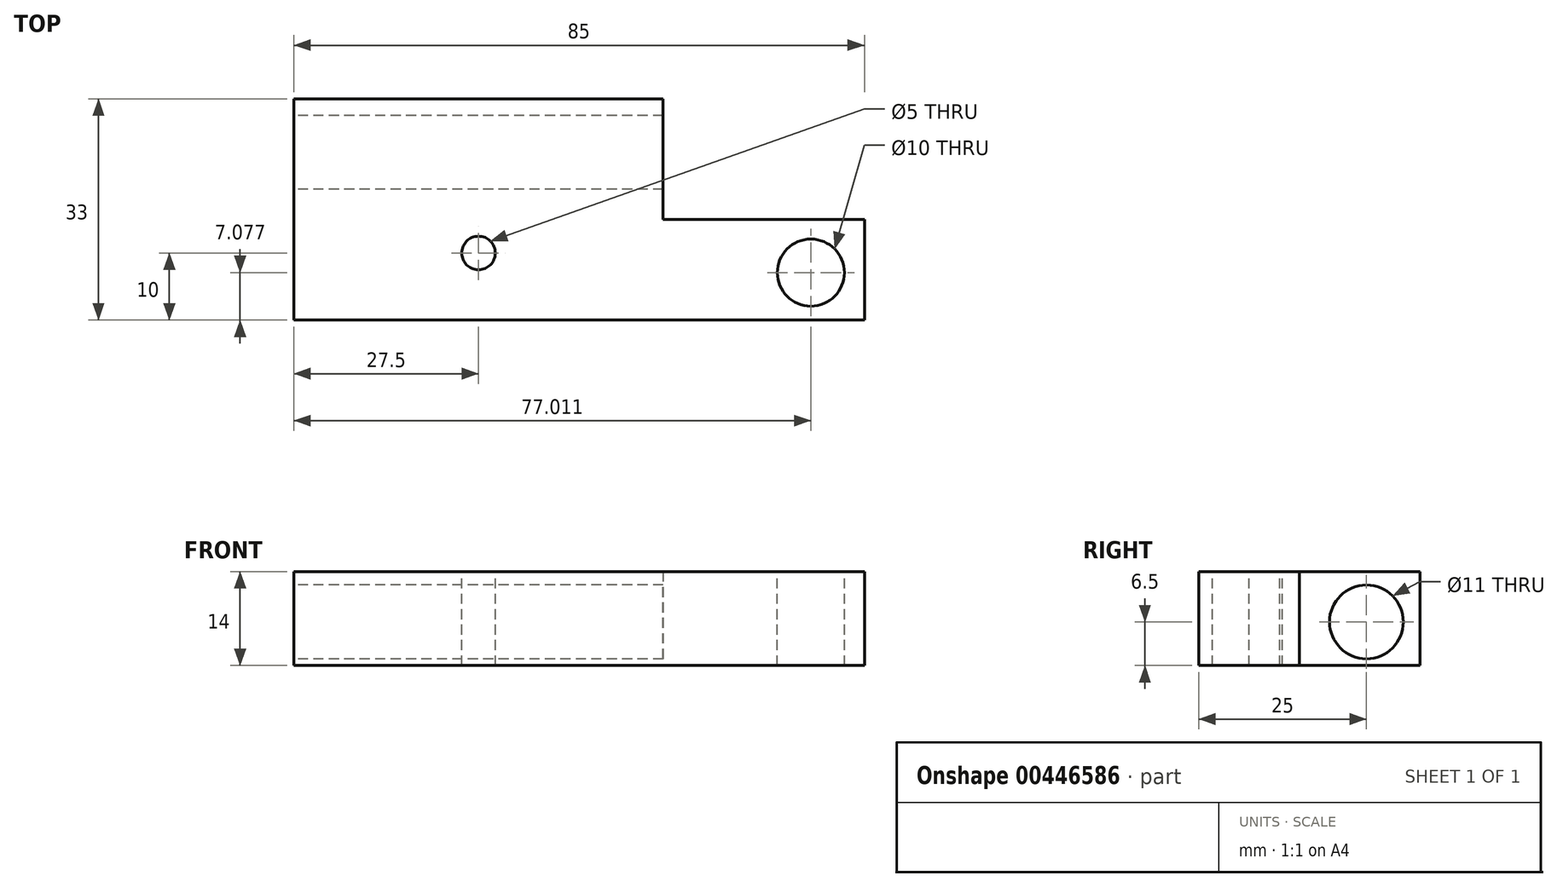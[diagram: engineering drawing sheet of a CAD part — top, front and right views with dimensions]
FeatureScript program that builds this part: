
annotation { "Feature Type Name" : "Feature", "Feature Type Description" : "" }
export const myFeature = defineFeature(function(context is Context, id is Id, definition is map)
    precondition{}
    {
        {
            var Q0;
            Q0=qCreatedBy(makeId("Top.planeOp"),FACE);
            var sketch = newSketch(context, id + "F0", { "sketchPlane" : qUnion([Q0])});
            skLineSegment(sketch, "E0.bottom", {"start": v(-27.5, 25) * mm, "end": v(27.5, 25) * mm});
            skLineSegment(sketch, "E0.top", {"start": v(-27.5, -25) * mm, "end": v(27.5, -25) * mm});
            skLineSegment(sketch, "E0.left", {"start": v(-27.5, 25) * mm, "end": v(-27.5, -25) * mm});
            skLineSegment(sketch, "E0.right", {"start": v(27.5, 25) * mm, "end": v(27.5, -25) * mm});
            skPoint(sketch, "E0.middle", {"position": v(0, 0) * mm});
            skLineSegment(sketch, "E1.bottom", {"start": v(27.5, -25) * mm, "end": v(57.5, -25) * mm});
            skLineSegment(sketch, "E1.top", {"start": v(27.5, -10) * mm, "end": v(57.5, -10) * mm});
            skLineSegment(sketch, "E1.left", {"start": v(27.5, -25) * mm, "end": v(27.5, -10) * mm});
            skLineSegment(sketch, "E1.right", {"start": v(57.5, -25) * mm, "end": v(57.5, -10) * mm});
            skSolve(sketch);
        }
        {
            var Q0;
            Q0 = qSketchRegion(id + "F0", true);
            extrude(context, id + "F1", {"entities" : qUnion([Q0]), "depth" : 14 * mm});
        }
        {
            var Q0;
            Q0=makeQuery(id+"F1.opExtrude","SWEPT_FACE",FACE,{"disambiguationData":[OSD([sQuery(id+"F0.wireOp",EDGE,"E0.left")])]});
            var sketch = newSketch(context, id + "F2", { "sketchPlane" : qUnion([Q0])});
            skPoint(sketch, "E2.centerSnap0", {"position": v(25, 7) * mm});
            skPoint(sketch, "E2.centerSnap1", {"position": v(0, 14) * mm});
            skCircle(sketch, "E3.0", {"center": v(0, 6.5) * mm, "radius": 5.5 * mm});
            skSolve(sketch);
        }
        {
            var Q0;
            Q0=makeQuery(id+"F1.opExtrude","CAP_FACE",FACE,{"disambiguationData":[OSD([sQuery(id+"F0.wireOp",EDGE,"E0.bottom"),sQuery(id+"F0.wireOp",EDGE,"E0.top"),sQuery(id+"F0.wireOp",EDGE,"E0.left"),sQuery(id+"F0.wireOp",EDGE,"E0.right")])],"isStart":false});
            var sketch = newSketch(context, id + "F3", { "sketchPlane" : qUnion([Q0])});
            skCircle(sketch, "E4", {"center": v(0, -15) * mm, "radius": 2.5 * mm});
            skSolve(sketch);
        }
        {
            var Q0;
            Q0 = qSketchRegion(id + "F3", true);
            extrude(context, id + "F4", {"entities" : qUnion([Q0]), "operationType" : NewBodyOperationType.REMOVE, "endBound" : BoundingType.THROUGH_ALL, "oppositeDirection" : true, "depth" : 25 * mm});
        }
        {
            var Q0;
            Q0=makeQuery(id+"F1.opExtrude","CAP_FACE",FACE,{"disambiguationData":[OSD([sQuery(id+"F0.wireOp",EDGE,"E0.bottom"),sQuery(id+"F0.wireOp",EDGE,"E0.top"),sQuery(id+"F0.wireOp",EDGE,"E0.left"),sQuery(id+"F0.wireOp",EDGE,"E0.right"),sQuery(id+"F0.wireOp",EDGE,"E1.bottom"),sQuery(id+"F0.wireOp",EDGE,"E1.top"),sQuery(id+"F0.wireOp",EDGE,"E1.right")])],"isStart":false});
            var sketch = newSketch(context, id + "F5", { "sketchPlane" : qUnion([Q0])});
            skCircle(sketch, "E5", {"center": v(49.51, -17.92) * mm, "radius": 5 * mm});
            skSolve(sketch);
        }
        {
            var Q0;
            Q0 = qSketchRegion(id + "F5", true);
            extrude(context, id + "F6", {"entities" : qUnion([Q0]), "operationType" : NewBodyOperationType.REMOVE, "endBound" : BoundingType.THROUGH_ALL, "oppositeDirection" : true, "depth" : 25 * mm});
        }
        {
            var Q0;
            Q0=makeQuery(id+"F1.opExtrude","CAP_FACE",FACE,{"disambiguationData":[OSD([sQuery(id+"F0.wireOp",EDGE,"E0.bottom"),sQuery(id+"F0.wireOp",EDGE,"E0.top"),sQuery(id+"F0.wireOp",EDGE,"E0.left"),sQuery(id+"F0.wireOp",EDGE,"E0.right"),sQuery(id+"F0.wireOp",EDGE,"E1.bottom"),sQuery(id+"F0.wireOp",EDGE,"E1.top"),sQuery(id+"F0.wireOp",EDGE,"E1.right")])],"isStart":true});
            var sketch = newSketch(context, id + "F7", { "sketchPlane" : qUnion([Q0])});
            skLineSegment(sketch, "E6.bottom", {"start": v(27.5, -25) * mm, "end": v(-27.5, -25) * mm});
            skLineSegment(sketch, "E6.top", {"start": v(27.5, -8) * mm, "end": v(-27.5, -8) * mm});
            skLineSegment(sketch, "E6.left", {"start": v(27.5, -25) * mm, "end": v(27.5, -8) * mm});
            skLineSegment(sketch, "E6.right", {"start": v(-27.5, -25) * mm, "end": v(-27.5, -8) * mm});
            skSolve(sketch);
        }
        {
            var Q0;
            Q0 = qSketchRegion(id + "F7", true);
            extrude(context, id + "F8", {"entities" : qUnion([Q0]), "operationType" : NewBodyOperationType.REMOVE, "endBound" : BoundingType.THROUGH_ALL, "oppositeDirection" : true, "depth" : 25 * mm});
        }
        {
            var Q0;
            Q0 = qSketchRegion(id + "F2", true);
            extrude(context, id + "F9", {"entities" : qUnion([Q0]), "operationType" : NewBodyOperationType.REMOVE, "endBound" : BoundingType.THROUGH_ALL, "oppositeDirection" : true, "depth" : 25 * mm});
        }
    });
